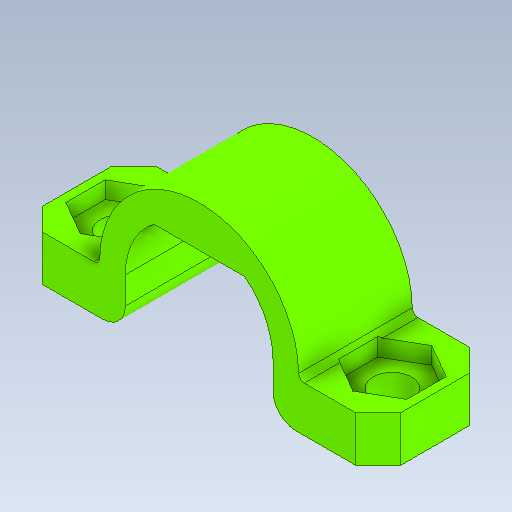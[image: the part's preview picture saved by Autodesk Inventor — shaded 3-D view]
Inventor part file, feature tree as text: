
AUTODESK INVENTOR PART (.ipt)
format: ipt  version: 2020 (Build 240168000, 168)  size: 191,488 bytes
history: native  units: mm
features: extrude x4, sketch x2, chamfer x1
ambient origin geometry x8: Origin, YZ Plane, XZ Plane, XY Plane, X Axis, Y Axis, Z Axis, Center Point
bodies: Solid1 (feature_tree)
feature tree (7):
  extrude  "Extrusion1"  Depth=2.0mm
  chamfer  "Chamfer1"  Distance=0.5mm
  sketch  "Sketch2"  dims[d6=6.5mm d7=0.5mm d9=0.5mm d10=4.0mm d11=6.5mm d12=6.5mm d13=10.0mm d14=25.0mm d15=10.0mm d16=0.0mm d17=2.0mm d18=2.0mm d19=45.0deg d20=24.0mm d21=3.4mm d22=6.0mm d23=10.0mm d24=0.0mm d25=0.0mm d26=0.0mm d27=1.5mm d28=0.0mm]
  extrude  "Extrusion2"  Depth=0.5mm
  extrude  "Extrusion3"  Depth=4.0mm
  extrude  "Extrusion4"  Depth=6.5mm
  sketch  "Sketch1"  dims[d0=4.0mm d4=2.0mm]
